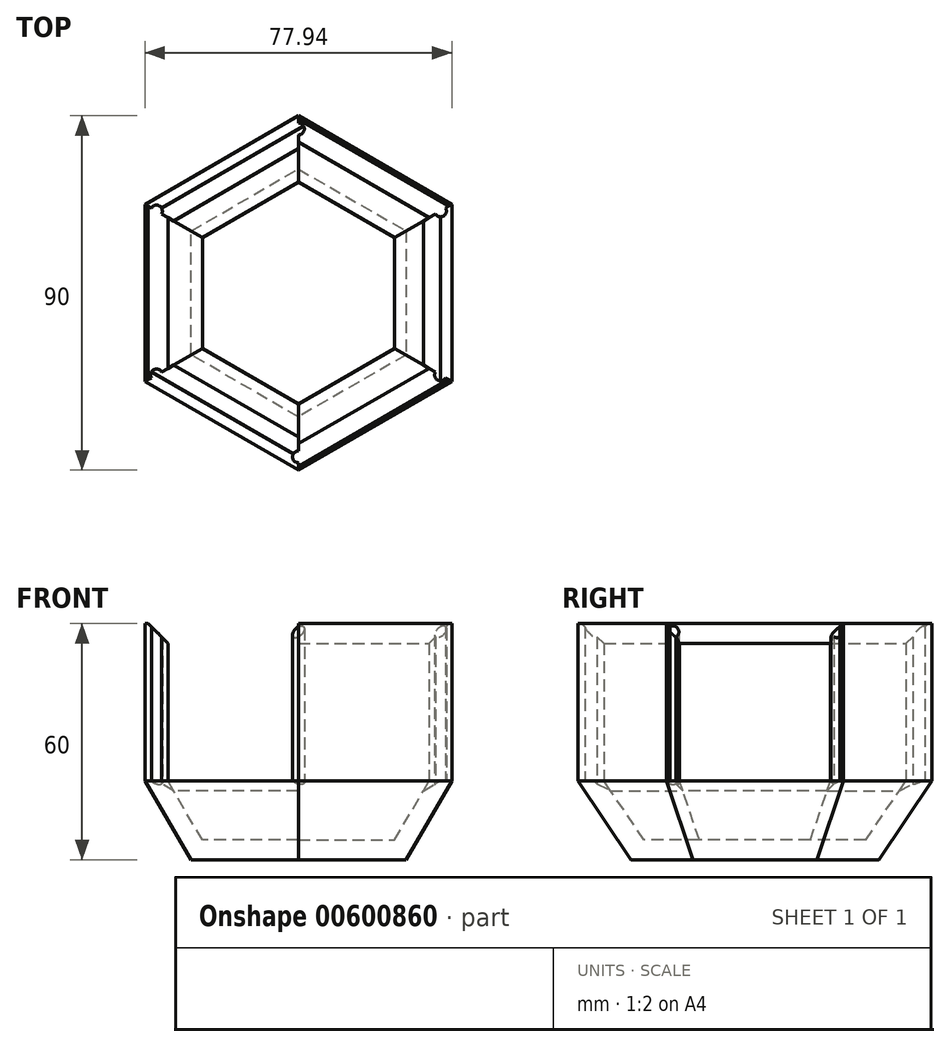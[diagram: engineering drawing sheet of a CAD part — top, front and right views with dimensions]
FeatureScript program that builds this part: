
annotation { "Feature Type Name" : "Feature", "Feature Type Description" : "" }
export const myFeature = defineFeature(function(context is Context, id is Id, definition is map)
    precondition{}
    {
        {
            var Q0;
            Q0=qCreatedBy(makeId("Top.planeOp"),FACE);
            var sketch = newSketch(context, id + "F0", { "sketchPlane" : qUnion([Q0])});
            skCircle(sketch, "E0.cCircle", {"center": v(0, 0) * mm, "radius": 31.5 * mm, "construction": true});
            skLineSegment(sketch, "E0.0", {"start": v(0, 31.5) * mm, "end": v(27.28, 15.75) * mm});
            skLineSegment(sketch, "E0.1", {"start": v(27.28, 15.75) * mm, "end": v(27.28, -15.75) * mm});
            skLineSegment(sketch, "E0.2", {"start": v(27.28, -15.75) * mm, "end": v(0, -31.5) * mm});
            skLineSegment(sketch, "E0.3", {"start": v(0, -31.5) * mm, "end": v(-27.28, -15.75) * mm});
            skLineSegment(sketch, "E0.4", {"start": v(-27.28, -15.75) * mm, "end": v(-27.28, 15.75) * mm});
            skLineSegment(sketch, "E0.5", {"start": v(-27.28, 15.75) * mm, "end": v(0, 31.5) * mm});
            skSolve(sketch);
        }
        {
            var Q0;
            Q0=makeQuery(id+"F0.imprint","IMPRINT",FACE,{"disambiguationData":[TD([[makeQuery(id+"F0.imprint","IMPRINT",EDGE,{"derivedFrom":sQuery(id+"F0.wireOp",EDGE,"E0.0")}),-1.0]])]});
            cPlane(context, id + "F1", {"entities" : qUnion([Q0]), "cplaneType" : CPlaneType.OFFSET, "offset" : 20 * mm, "width" : 150 * mm, "height" : 150 * mm});
        }
        {
            var Q0;
            Q0=qCreatedBy(id+"F1.planeOp",FACE);
            var sketch = newSketch(context, id + "F2", { "sketchPlane" : qUnion([Q0])});
            skCircle(sketch, "E1.cCircle", {"center": v(0, 0) * mm, "radius": 45 * mm, "construction": true});
            skLineSegment(sketch, "E1.0", {"start": v(0, -45) * mm, "end": v(-38.97, -22.5) * mm});
            skLineSegment(sketch, "E1.1", {"start": v(-38.97, -22.5) * mm, "end": v(-38.97, 22.5) * mm});
            skLineSegment(sketch, "E1.2", {"start": v(-38.97, 22.5) * mm, "end": v(0, 45) * mm});
            skLineSegment(sketch, "E1.3", {"start": v(0, 45) * mm, "end": v(38.97, 22.5) * mm});
            skLineSegment(sketch, "E1.4", {"start": v(38.97, 22.5) * mm, "end": v(38.97, -22.5) * mm});
            skLineSegment(sketch, "E1.5", {"start": v(38.97, -22.5) * mm, "end": v(0, -45) * mm});
            skSolve(sketch);
        }
        {
            var Q0;
            Q0=qCreatedBy(id+"F1.planeOp",FACE);
            cPlane(context, id + "F3", {"entities" : qUnion([Q0]), "cplaneType" : CPlaneType.OFFSET, "offset" : 40 * mm, "width" : 150 * mm, "height" : 150 * mm});
        }
        {
            var Q0;
            Q0=makeQuery(id+"F0.imprint","IMPRINT",FACE,{"disambiguationData":[TD([[makeQuery(id+"F0.imprint","IMPRINT",EDGE,{"derivedFrom":sQuery(id+"F0.wireOp",EDGE,"E0.0")}),-1.0]])]});
            var Q1;
            Q1=makeQuery(id+"F2.imprint","IMPRINT",FACE,{"disambiguationData":[TD([[makeQuery(id+"F2.imprint","IMPRINT",EDGE,{"derivedFrom":sQuery(id+"F2.wireOp",EDGE,"E1.0")}),-1.0]])]});
            loft(context, id + "F4", {"sheetProfilesArray" : [{ "sheetProfileEntities" : qUnion([Q0]) }, { "sheetProfileEntities" : qUnion([Q1]) }]});
        }
        {
            var Q0;
            Q0=makeQuery(id+"F4.opLoft","CAP_FACE",FACE,{"disambiguationData":[OSD([makeQuery(id+"F2.imprint","IMPRINT",FACE,{"disambiguationData":[TD([[makeQuery(id+"F2.imprint","IMPRINT",EDGE,{"derivedFrom":sQuery(id+"F2.wireOp",EDGE,"E1.0")}),-1.0]])]})])],"isStart":true});
            shell(context, id + "F5", {"entities" : qUnion([Q0]), "thickness" : 5 * mm});
        }
        {
            var Q0;
            Q0=makeQuery(id+"F4.opLoft","CAP_FACE",FACE,{"disambiguationData":[OSD([makeQuery(id+"F2.imprint","IMPRINT",FACE,{"disambiguationData":[TD([[makeQuery(id+"F2.imprint","IMPRINT",EDGE,{"derivedFrom":sQuery(id+"F2.wireOp",EDGE,"E1.0")}),-1.0]])]})])],"isStart":true});
            var sketch = newSketch(context, id + "F6", { "sketchPlane" : qUnion([Q0])});
            skLineSegment(sketch, "E2", {"start": v(-33.18, -19.16) * mm, "end": v(-33.18, 19.16) * mm});
            skLineSegment(sketch, "E3", {"start": v(-38.97, 22.5) * mm, "end": v(-38.97, -22.5) * mm});
            skArc(sketch, "E4.1.5", {"start": v(-34.78, -20.08) * mm, "mid": v(-36.83, -19.53) * mm, "end": v(-37.37, -21.58) * mm});
            skLineSegment(sketch, "E5", {"start": v(-38.97, -22.5) * mm, "end": v(-33.18, -19.16) * mm, "construction": true});
            skLineSegment(sketch, "E6", {"start": v(-38.97, -22.5) * mm, "end": v(-37.37, -21.58) * mm});
            skLineSegment(sketch, "E7", {"start": v(-33.18, -19.16) * mm, "end": v(-34.78, -20.08) * mm});
            skLineSegment(sketch, "E8", {"start": v(-38.97, 22.5) * mm, "end": v(-33.18, 19.16) * mm, "construction": true});
            skArc(sketch, "E9", {"start": v(-34.78, 20.08) * mm, "mid": v(-35.33, 22.13) * mm, "end": v(-37.37, 21.58) * mm});
            skLineSegment(sketch, "E10", {"start": v(-38.97, 22.5) * mm, "end": v(-37.37, 21.58) * mm});
            skLineSegment(sketch, "E11", {"start": v(-33.18, 19.16) * mm, "end": v(-34.78, 20.08) * mm});
            skLineSegment(sketch, "E12.1.0", {"start": v(0, -45) * mm, "end": v(38.97, -22.5) * mm});
            skLineSegment(sketch, "E12.1.1", {"start": v(33.18, -19.16) * mm, "end": v(0, -38.31) * mm});
            skArc(sketch, "E12.1.2", {"start": v(0, -40.16) * mm, "mid": v(-1.5, -41.66) * mm, "end": v(0, -43.16) * mm});
            skLineSegment(sketch, "E12.1.3", {"start": v(38.97, -22.5) * mm, "end": v(33.18, -19.16) * mm, "construction": true});
            skLineSegment(sketch, "E12.1.4", {"start": v(0, -45) * mm, "end": v(0, -38.31) * mm, "construction": true});
            skArc(sketch, "E12.1.5", {"start": v(34.78, -20.08) * mm, "mid": v(35.33, -22.13) * mm, "end": v(37.37, -21.58) * mm});
            skLineSegment(sketch, "E12.1.6", {"start": v(38.97, -22.5) * mm, "end": v(37.37, -21.58) * mm});
            skLineSegment(sketch, "E12.1.7", {"start": v(0, -45) * mm, "end": v(0, -43.16) * mm});
            skLineSegment(sketch, "E12.1.8", {"start": v(33.18, -19.16) * mm, "end": v(34.78, -20.08) * mm});
            skLineSegment(sketch, "E12.1.9", {"start": v(0, -38.31) * mm, "end": v(0, -40.16) * mm});
            skLineSegment(sketch, "E12.2.0", {"start": v(38.97, 22.5) * mm, "end": v(0, 45) * mm});
            skLineSegment(sketch, "E12.2.1", {"start": v(0, 38.31) * mm, "end": v(33.18, 19.16) * mm});
            skArc(sketch, "E12.2.2", {"start": v(34.78, 20.08) * mm, "mid": v(36.83, 19.53) * mm, "end": v(37.37, 21.58) * mm});
            skLineSegment(sketch, "E12.2.3", {"start": v(0, 45) * mm, "end": v(0, 38.31) * mm, "construction": true});
            skLineSegment(sketch, "E12.2.4", {"start": v(38.97, 22.5) * mm, "end": v(33.18, 19.16) * mm, "construction": true});
            skArc(sketch, "E12.2.5", {"start": v(0, 40.16) * mm, "mid": v(1.5, 41.66) * mm, "end": v(0, 43.16) * mm});
            skLineSegment(sketch, "E12.2.6", {"start": v(0, 45) * mm, "end": v(0, 43.16) * mm});
            skLineSegment(sketch, "E12.2.7", {"start": v(38.97, 22.5) * mm, "end": v(37.37, 21.58) * mm});
            skLineSegment(sketch, "E12.2.8", {"start": v(0, 38.31) * mm, "end": v(0, 40.16) * mm});
            skLineSegment(sketch, "E12.2.9", {"start": v(33.18, 19.16) * mm, "end": v(34.78, 20.08) * mm});
            skPoint(sketch, "E12.center", {"position": v(0, 0) * mm});
            skSolve(sketch);
        }
        {
            var Q0;
            Q0=makeQuery(id+"F6.imprint","IMPRINT",FACE,{"disambiguationData":[TD([[makeQuery(id+"F6.imprint","IMPRINT",EDGE,{"derivedFrom":sQuery(id+"F6.wireOp",EDGE,"E2")}),-1.0]])]});
            var Q1;
            Q1=makeQuery(id+"F6.imprint","IMPRINT",FACE,{"disambiguationData":[TD([[makeQuery(id+"F6.imprint","IMPRINT",EDGE,{"derivedFrom":sQuery(id+"F6.wireOp",EDGE,"E12.2.0")}),1.0]])]});
            var Q2;
            Q2=makeQuery(id+"F6.imprint","IMPRINT",FACE,{"disambiguationData":[TD([[makeQuery(id+"F6.imprint","IMPRINT",EDGE,{"derivedFrom":sQuery(id+"F6.wireOp",EDGE,"E12.1.0")}),1.0]])]});
            extrude(context, id + "F7", {"entities" : qUnion([Q0, Q1, Q2]), "operationType" : NewBodyOperationType.ADD, "depth" : 40 * mm, "offsetDistance" : 25 * mm});
        }
        {
            var Q0;
            Q0=makeQuery(id+"F7.opExtrude","CAP_EDGE",EDGE,{"disambiguationData":[OSD([sQuery(id+"F6.wireOp",EDGE,"E12.1.1")])],"isStart":false});
            var Q1;
            Q1=makeQuery(id+"F5.opShell","OFFSET_EDGE",EDGE,{"disambiguationData":[OSD([sQuery(id+"F2.wireOp",EDGE,"E1.3"),sQuery(id+"F2.wireOp",EDGE,"E1.4"),sQuery(id+"F2.wireOp",EDGE,"E1.5")])]});
            var Q2;
            Q2=makeQuery(id+"F5.opShell","OFFSET_EDGE",EDGE,{"disambiguationData":[OSD([sQuery(id+"F2.wireOp",EDGE,"E1.1"),sQuery(id+"F2.wireOp",EDGE,"E1.2"),sQuery(id+"F2.wireOp",EDGE,"E1.3")])]});
            var Q3;
            Q3=makeQuery(id+"F5.opShell","OFFSET_EDGE",EDGE,{"disambiguationData":[OSD([sQuery(id+"F2.wireOp",EDGE,"E1.0"),sQuery(id+"F2.wireOp",EDGE,"E1.1"),sQuery(id+"F2.wireOp",EDGE,"E1.5")])]});
            var Q4;
            Q4=makeQuery(id+"F7.opExtrude","CAP_EDGE",EDGE,{"disambiguationData":[OSD([sQuery(id+"F6.wireOp",EDGE,"E2")])],"isStart":false});
            var Q5;
            Q5=makeQuery(id+"F7.opExtrude","CAP_EDGE",EDGE,{"disambiguationData":[OSD([sQuery(id+"F6.wireOp",EDGE,"E12.2.1")])],"isStart":false});
            chamfer(context, id + "F8", {"entities" : qUnion([Q0, Q1, Q2, Q3, Q4, Q5]), "width" : 5 * mm, "tangentPropagation" : true});
        }
    });
